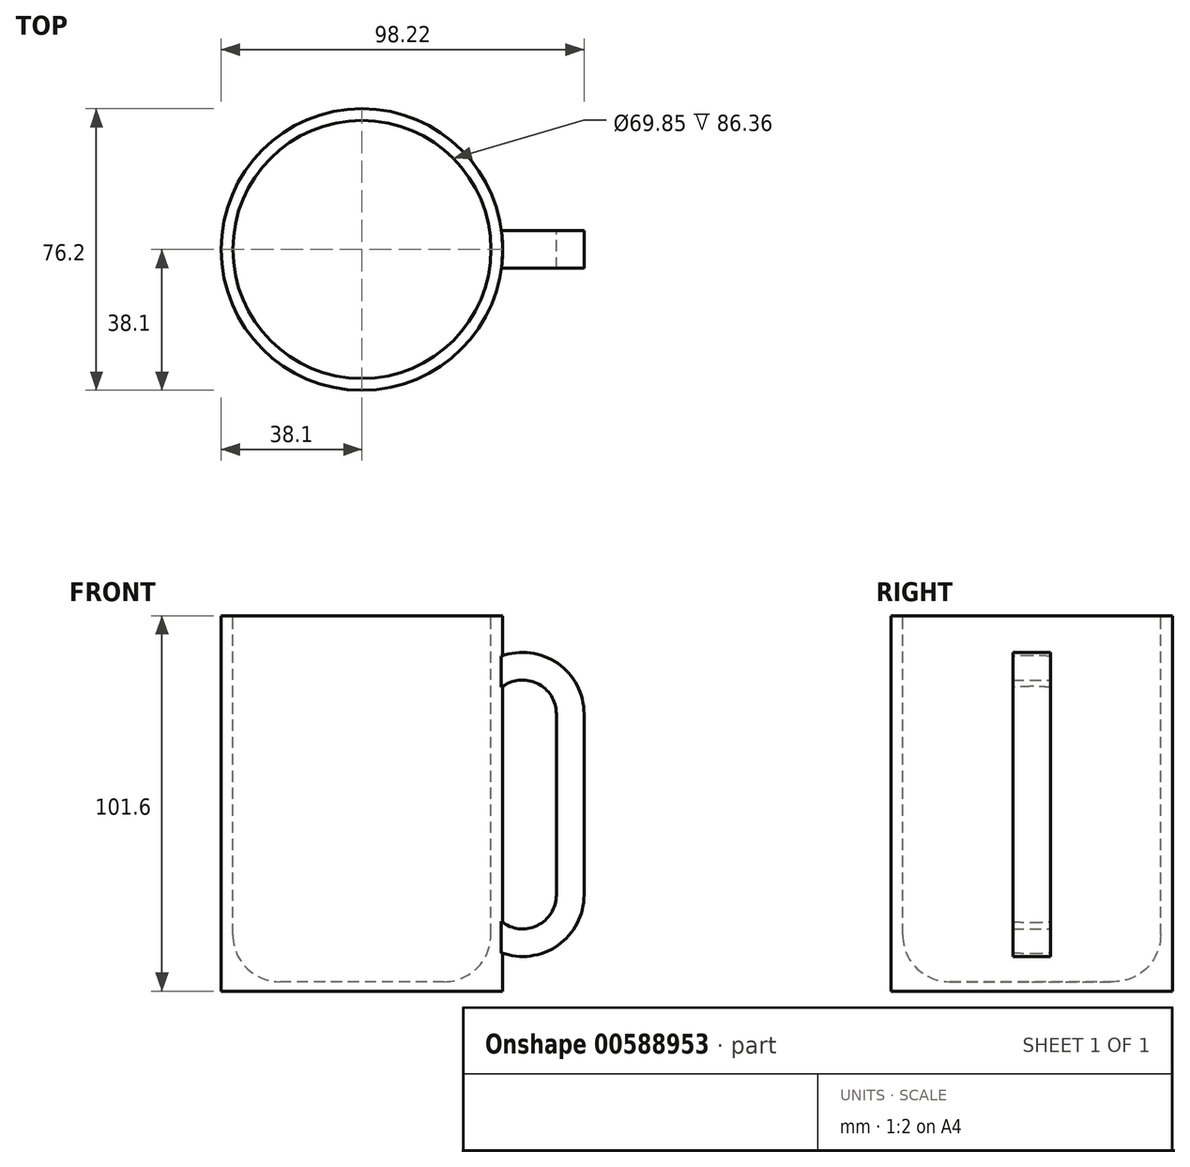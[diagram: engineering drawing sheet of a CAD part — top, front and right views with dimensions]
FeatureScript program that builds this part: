
annotation { "Feature Type Name" : "Feature", "Feature Type Description" : "" }
export const myFeature = defineFeature(function(context is Context, id is Id, definition is map)
    precondition{}
    {
        {
            var Q0;
            Q0=qCreatedBy(makeId("Top.planeOp"),FACE);
            var sketch = newSketch(context, id + "F0", { "sketchPlane" : qUnion([Q0])});
            skCircle(sketch, "E0", {"center": v(0, 0) * mm, "radius": 38.1 * mm});
            skSolve(sketch);
        }
        {
            var Q0;
            Q0 = qSketchRegion(id + "F0", true);
            extrude(context, id + "F1", {"entities" : qUnion([Q0]), "depth" : 50.8 * mm, "offsetDistance" : 25.4 * mm, "hasSecondDirection" : true, "secondDirectionOppositeDirection" : true, "secondDirectionDepth" : 50.8 * mm});
        }
        {
            var Q0;
            Q0=makeQuery(id+"F1.opExtrude","CAP_FACE",FACE,{"disambiguationData":[OSD([sQuery(id+"F0.wireOp",EDGE,"E0")])],"isStart":false});
            var sketch = newSketch(context, id + "F2", { "sketchPlane" : qUnion([Q0])});
            skCircle(sketch, "E1", {"center": v(0, 0) * mm, "radius": 34.93 * mm});
            skSolve(sketch);
        }
        {
            var Q0;
            Q0=makeQuery(id+"F2.imprint","IMPRINT",FACE,{"disambiguationData":[TD([[makeQuery(id+"F2.imprint","IMPRINT",EDGE,{"derivedFrom":sQuery(id+"F2.wireOp",EDGE,"E1")}),1.0]])]});
            extrude(context, id + "F3", {"entities" : qUnion([Q0]), "operationType" : NewBodyOperationType.REMOVE, "oppositeDirection" : true, "depth" : 99.06 * mm, "offsetDistance" : 25.4 * mm});
        }
        {
            var Q0;
            Q0=qCreatedBy(makeId("Front.planeOp"),FACE);
            var sketch = newSketch(context, id + "F4", { "sketchPlane" : qUnion([Q0])});
            skArc(sketch, "E2", {"start": v(60.12, 24.24) * mm, "mid": v(52.1, 38.46) * mm, "end": v(35.8, 38.98) * mm});
            skLineSegment(sketch, "E3", {"start": v(60.12, 24.24) * mm, "end": v(60.12, -24.8) * mm});
            skArc(sketch, "E4", {"start": v(35.8, -39.54) * mm, "mid": v(52.1, -39.02) * mm, "end": v(60.12, -24.8) * mm});
            skLineSegment(sketch, "E5", {"start": v(52.65, 24.24) * mm, "end": v(52.65, -24.8) * mm});
            skArc(sketch, "E6", {"start": v(52.65, 24.24) * mm, "mid": v(46.08, 33.02) * mm, "end": v(35.8, 29.2) * mm});
            skArc(sketch, "E7", {"start": v(35.8, -29.77) * mm, "mid": v(46.08, -33.59) * mm, "end": v(52.65, -24.8) * mm});
            skLineSegment(sketch, "E8", {"start": v(35.8, 38.98) * mm, "end": v(35.8, 29.2) * mm});
            skLineSegment(sketch, "E9", {"start": v(35.8, -39.54) * mm, "end": v(35.8, -29.77) * mm});
            skSolve(sketch);
        }
        {
            var Q0;
            Q0 = qSketchRegion(id + "F4", true);
            extrude(context, id + "F5", {"entities" : qUnion([Q0]), "operationType" : NewBodyOperationType.ADD, "depth" : 5.08 * mm, "offsetDistance" : 25.4 * mm, "hasSecondDirection" : true, "secondDirectionOppositeDirection" : true, "secondDirectionDepth" : 5.08 * mm});
        }
        {
            var Q0;
            Q0=makeQuery(id+"F3.boolean.opBoolean","COPY",EDGE,{"derivedFrom":makeQuery(id+"F3.opExtrude","CAP_EDGE",EDGE,{"disambiguationData":[OSD([sQuery(id+"F2.wireOp",EDGE,"E1")])],"isStart":false})});
            fillet(context, id + "F6", {"entities" : qUnion([Q0]), "radius" : 12.7 * mm, "tangentPropagation" : true, "allowEdgeOverflow" : false});
        }
    });
